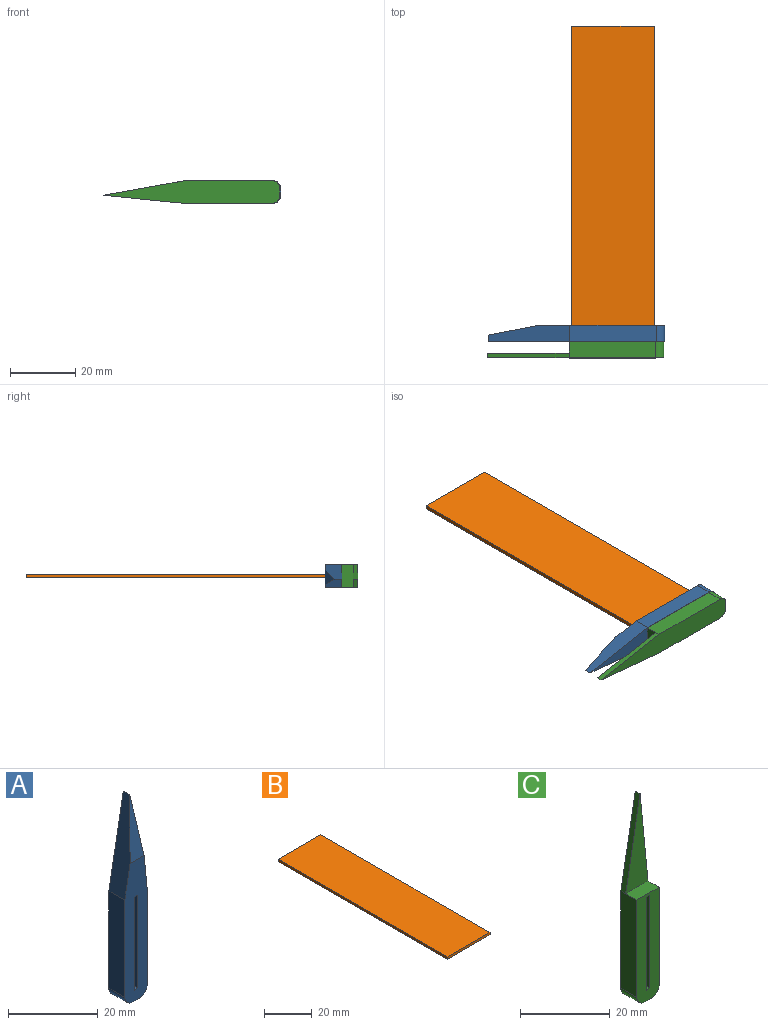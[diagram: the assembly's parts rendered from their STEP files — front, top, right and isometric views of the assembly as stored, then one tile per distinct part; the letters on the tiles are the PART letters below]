
ASSEMBLY  parts=3 mates=5
PART A: 14 faces, bbox 7x5x54 mm
  f0: plane 38.2x7mm, normal (0,-1,0), area 222.4mm2, adj f2,f3,f4,f5,f6,f7,f8,f9
  f1: plane 54x7mm, normal (0,1,0), area 257.3mm2, adj f2,f3,f4,f5,f6,f7,f8,f9
  f2: plane 26.5x5mm, normal (1,0,0), area 132.5mm2, adj f0,f1,f3,f12
  f3: plane 25x5mm, normal (1,0,0.1), area 101.8mm2, adj f0,f1,f2,f4,f13
  f4: plane 25x5mm, normal (-0.98,0,0.18), area 102.9mm2, adj f0,f1,f3,f5,f13
  f5: plane 26.5x5mm, normal (-1,0,0), area 132.5mm2, adj f0,f1,f4,f11
  f6: plane 5x2mm, normal (0,0,-1), area 10mm2, adj f0,f1,f11,f12
  f7: plane 25.4x5mm, normal (1,0,0), area 127mm2, adj f0,f1,f8,f10
  f8: plane 5x1.2mm, normal (0,0,1), area 6mm2, adj f0,f1,f7,f9
  f9: plane 25.4x5mm, normal (-1,0,0), area 127mm2, adj f0,f1,f8,f10
  f10: plane 5x1.2mm, normal (0,0,-1), area 6mm2, adj f0,f1,f7,f9
  f11: cylinder r=2.5mm len=5mm, axis (0,-1,0), area 19.6mm2, adj f0,f1,f5,f6
  f12: cylinder r=2.5mm len=5mm, axis (0,1,0), area 19.6mm2, adj f0,f1,f2,f6
  f13: plane 15.8x4.43mm, normal (0,-0.98,0.19), area 35.6mm2, adj f0,f3,f4
PART B: 6 faces, bbox 25.2x100x1.2 mm
  f0: plane 100x1.2mm, normal (-1,0,0), area 120mm2, adj f1,f3,f4,f5
  f1: plane 100x25.2mm, normal (0,0,-1), area 2520mm2, adj f0,f2,f4,f5
  f2: plane 100x1.2mm, normal (1,0,0), area 120mm2, adj f1,f3,f4,f5
  f3: plane 100x25.2mm, normal (0,0,1), area 2520mm2, adj f0,f2,f4,f5
  f4: plane 25.2x1.2mm, normal (0,-1,0), area 30.2mm2, adj f0,f1,f2,f3
  f5: plane 25.2x1.2mm, normal (0,1,0), area 30.2mm2, adj f0,f1,f2,f3
PART C: 16 faces, bbox 7x5x54 mm
  f0: plane 25x2.5mm, normal (1,0,0.1), area 37.7mm2, adj f1,f3,f6,f13
  f1: plane 25x4.5mm, normal (-0.98,0,0.18), area 38.1mm2, adj f0,f4,f6,f13
  f2: plane 29x7mm, normal (0,-1,0), area 169.8mm2, adj f3,f4,f5,f7,f8,f9,f10,f12
  f3: plane 26.5x5mm, normal (1,0,0), area 132.5mm2, adj f0,f2,f6,f12,f15
  f4: plane 26.5x5mm, normal (-1,0,0), area 132.5mm2, adj f1,f2,f6,f12,f14
  f5: plane 5x2mm, normal (0,0,-1), area 10mm2, adj f2,f6,f14,f15
  f6: plane 54x7mm, normal (0,1,0), area 287.8mm2, adj f0,f1,f3,f4,f5,f14,f15
  f7: plane 25.4x3.5mm, normal (1,0,0), area 88.9mm2, adj f2,f8,f10,f11
  f8: plane 3.5x1.2mm, normal (0,0,1), area 4.2mm2, adj f2,f7,f9,f11
  f9: plane 25.4x3.5mm, normal (-1,0,0), area 88.9mm2, adj f2,f8,f10,f11
  f10: plane 3.5x1.2mm, normal (0,0,-1), area 4.2mm2, adj f2,f7,f9,f11
  f11: plane 25.4x1.2mm, normal (0,-1,0), area 30.5mm2, adj f7,f8,f9,f10
  f12: plane 7x3.5mm, normal (0,0,1), area 24.5mm2, adj f2,f3,f4,f13
  f13: plane 25x7mm, normal (0,-1,0), area 87.5mm2, adj f0,f1,f12
  f14: cylinder r=2.5mm len=5mm, axis (0,-1,0), area 19.6mm2, adj f2,f4,f5,f6
  f15: cylinder r=2.5mm len=5mm, axis (0,1,0), area 19.6mm2, adj f2,f3,f5,f6
PLACE A rot(axis=(0.71,0,-0.71),180deg) t=(28.4,3.52,2.9)mm
PLACE B t=(0,100,-1.2)mm
PLACE C rot(axis=(0.71,0,-0.71),180deg) t=(28.2,-1.5,2.9)mm
MATE planar C.f9 <-> B.f1  axis (0,0,1) through (-0.2,1.75,-1.2)mm
MATE planar C.f13 <-> B.f4  axis (0,1,0) through (-13.3,0,-2.85)mm
MATE planar A.f10 <-> B.f0  axis (1,0,0) through (0,6.02,-0.6)mm
MATE planar A.f9 <-> B.f1  axis (0,0,1) through (12.7,6.02,-1.2)mm
MATE planar C.f8 <-> B.f2  axis (-1,0,0) through (25.2,1.75,-0.6)mm
